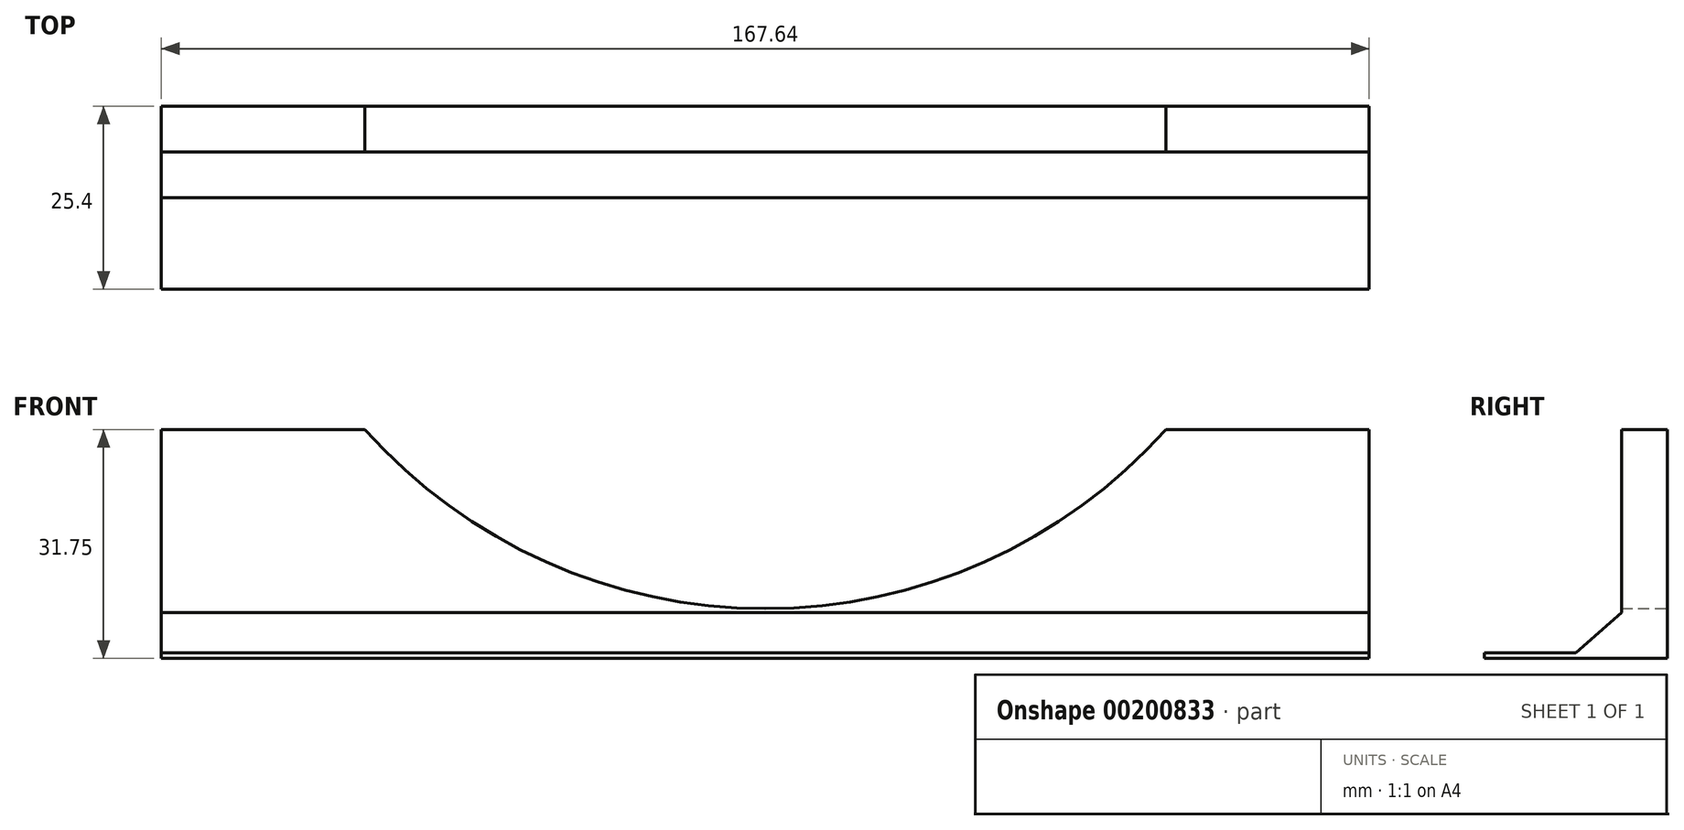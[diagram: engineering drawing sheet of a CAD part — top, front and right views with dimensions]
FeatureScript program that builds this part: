
annotation { "Feature Type Name" : "Feature", "Feature Type Description" : "" }
export const myFeature = defineFeature(function(context is Context, id is Id, definition is map)
    precondition{}
    {
        {
            var Q0;
            Q0=qCreatedBy(makeId("Front.planeOp"),FACE);
            var sketch = newSketch(context, id + "F0", { "sketchPlane" : qUnion([Q0])});
            skArc(sketch, "E0", {"start": v(-55.6, -49.76) * mm, "mid": v(0, -74.61) * mm, "end": v(55.6, -49.76) * mm});
            skLineSegment(sketch, "E1.top", {"start": v(-83.82, -81.51) * mm, "end": v(83.82, -81.51) * mm});
            skLineSegment(sketch, "E1.left", {"start": v(-83.82, -49.76) * mm, "end": v(-83.82, -81.51) * mm});
            skLineSegment(sketch, "E1.right", {"start": v(83.82, -49.76) * mm, "end": v(83.82, -81.51) * mm});
            skLineSegment(sketch, "E2.bottom", {"start": v(83.82, -49.76) * mm, "end": v(55.6, -49.76) * mm});
            skLineSegment(sketch, "E2.top", {"start": v(83.82, -81.51) * mm, "end": v(-83.82, -81.51) * mm});
            skPoint(sketch, "E3.orphan", {"position": v(-83.82, 0) * mm});
            skLineSegment(sketch, "E4.trimOffspring", {"start": v(-55.6, -49.76) * mm, "end": v(-83.82, -49.76) * mm});
            skSolve(sketch);
        }
        {
            var Q0;
            Q0 = qSketchRegion(id + "F0", true);
            extrude(context, id + "F1", {"entities" : qUnion([Q0]), "endBound" : BoundingType.SYMMETRIC, "depth" : 6.35 * mm});
        }
        {
            var Q0;
            Q0=makeQuery(id+"F1.opExtrude","SWEPT_FACE",FACE,{"disambiguationData":[OSD([sQuery(id+"F0.wireOp",EDGE,"E1.right")])]});
            var sketch = newSketch(context, id + "F2", { "sketchPlane" : qUnion([Q0])});
            skLineSegment(sketch, "E5", {"start": v(-3.18, -75.16) * mm, "end": v(-9.52, -80.75) * mm});
            skLineSegment(sketch, "E6", {"start": v(-10.4, -81.51) * mm, "end": v(-3.18, -81.51) * mm});
            skLineSegment(sketch, "E7.bottom", {"start": v(-9.53, -80.75) * mm, "end": v(-22.23, -80.75) * mm});
            skLineSegment(sketch, "E7.top", {"start": v(-10.4, -81.51) * mm, "end": v(-22.23, -81.51) * mm});
            skLineSegment(sketch, "E7.right", {"start": v(-22.23, -80.75) * mm, "end": v(-22.23, -81.51) * mm});
            skLineSegment(sketch, "E8", {"start": v(-3.17, -75.16) * mm, "end": v(-3.17, -81.51) * mm});
            skSolve(sketch);
        }
        {
            var Q0;
            Q0 = qSketchRegion(id + "F2", true);
            var Q1;
            Q1=makeQuery(id+"F1.opExtrude","SWEPT_FACE",FACE,{"disambiguationData":[OSD([sQuery(id+"F0.wireOp",EDGE,"E1.left")])]});
            extrude(context, id + "F3", {"entities" : qUnion([Q0]), "operationType" : NewBodyOperationType.ADD, "endBound" : BoundingType.UP_TO_SURFACE, "oppositeDirection" : true, "endBoundEntityFace" : qUnion([Q1]), "depth" : 25.4 * mm});
        }
    });
